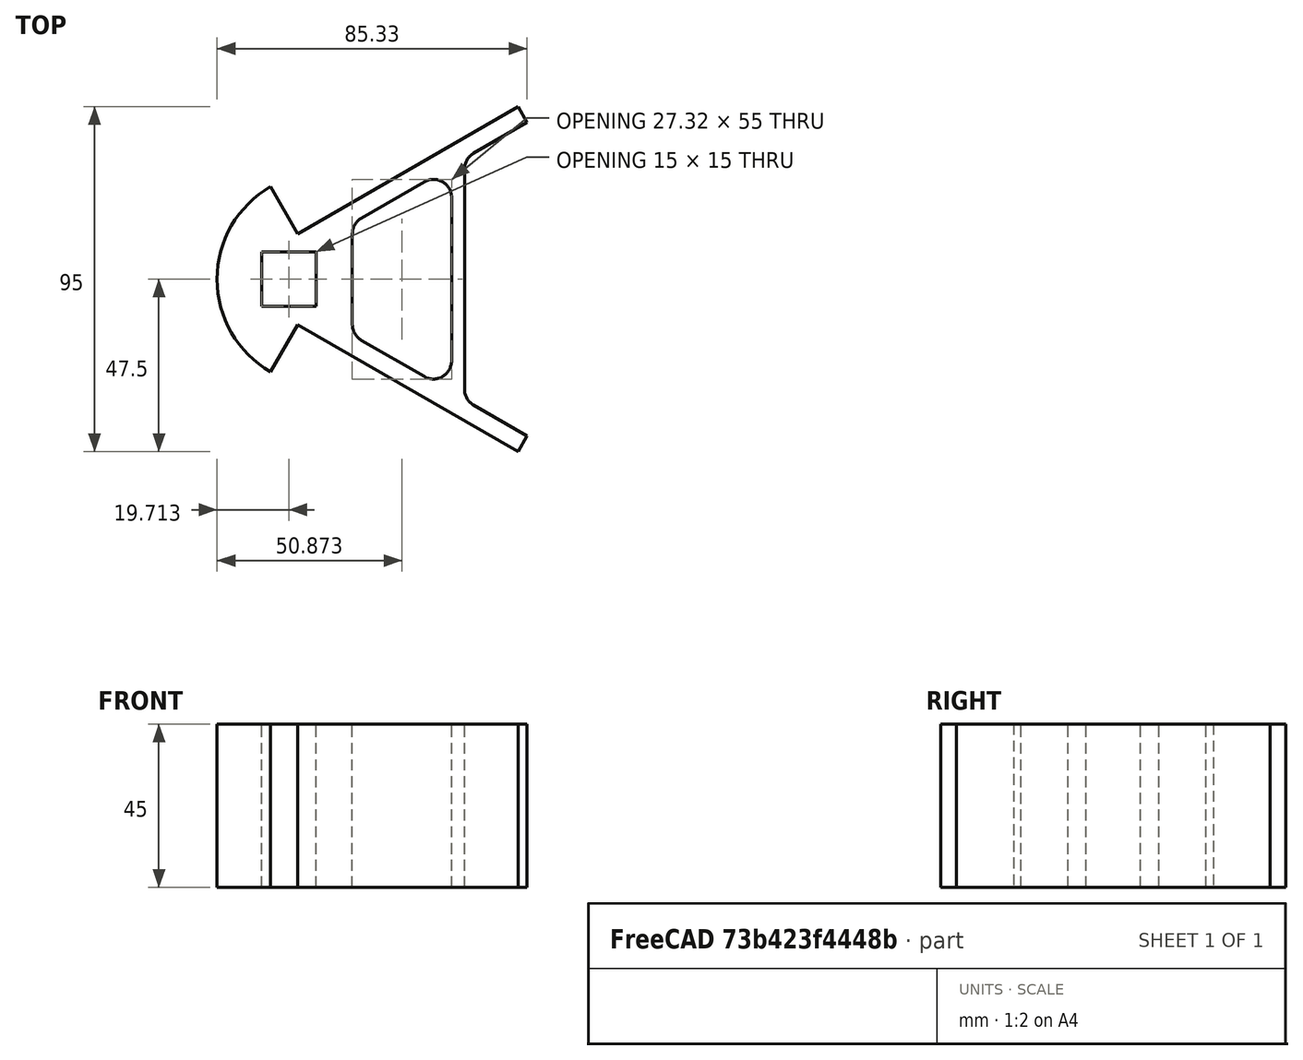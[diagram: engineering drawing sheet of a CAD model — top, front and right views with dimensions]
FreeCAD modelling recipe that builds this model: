
FCSTD DOCUMENT
Label: BaseCorner
objects: Sketcher::SketchObject×1, PartDesign::Pad×1
note: 3 computed .brp shape members not serialized (recipe doc carries the construction recipe); baked Part::Feature solids carry a one-line shape summary decoded from their .brp

FEATURE [Sketcher::SketchObject] Sketch
  sketch-geometry (32):
    g0: LineSegment StartX=-7.21688 StartY=60 StartZ=0 EndX=53.4049 EndY=95 EndZ=0
    g1: LineSegment StartX=-7.21688 StartY=35 StartZ=0 EndX=53.4049 EndY=0 EndZ=0
    g2: LineSegment StartX=53.4049 StartY=95 StartZ=0 EndX=55.9049 EndY=90.6699 EndZ=0
    g3: LineSegment StartX=53.4049 StartY=0 StartZ=0 EndX=55.9049 EndY=4.33013 EndZ=0
    g4: LineSegment StartX=55.9049 StartY=90.6699 StartZ=0 EndX=41.1552 EndY=82.1541 EndZ=0
    g5: LineSegment StartX=41.1552 StartY=12.8459 StartZ=0 EndX=55.9049 EndY=4.33013 EndZ=0
    g6: LineSegment StartX=27.6036 StartY=20.6699 StartZ=0 EndX=10.2831 EndY=30.6699 EndZ=0
    g7: LineSegment StartX=10.2831 StartY=64.3301 StartZ=0 EndX=27.6036 EndY=74.3301 EndZ=0
    g8: LineSegment [constr] StartX=27.6036 StartY=74.3301 StartZ=0 EndX=41.1552 EndY=82.1541 EndZ=0
    g9: LineSegment [constr] StartX=27.6036 StartY=20.6699 StartZ=0 EndX=41.1552 EndY=12.8459 EndZ=0
    g10: ArcOfCircle CenterX=30.1036 CenterY=70 CenterZ=0 NormalX=0 NormalY=0 NormalZ=1 Radius=5 StartAngle=1.02985e-06 EndAngle=2.09439
    g11: ArcOfCircle CenterX=30.1036 CenterY=25 CenterZ=0 NormalX=0 NormalY=0 NormalZ=1 Radius=5 StartAngle=4.18879 EndAngle=6.28318
    g12: LineSegment StartX=35.1036 StartY=70 StartZ=0 EndX=35.1036 EndY=25 EndZ=0
    g13: ArcOfCircle CenterX=12.7831 CenterY=60 CenterZ=0 NormalX=0 NormalY=0 NormalZ=1 Radius=5 StartAngle=2.09439 EndAngle=3.14159
    g14: ArcOfCircle CenterX=12.7831 CenterY=35 CenterZ=0 NormalX=0 NormalY=0 NormalZ=1 Radius=5 StartAngle=3.14159 EndAngle=4.1888
    g15: LineSegment StartX=7.7831 StartY=60 StartZ=0 EndX=7.7831 EndY=35 EndZ=0
    g16: LineSegment [constr] StartX=-14.7169 StartY=72.9904 StartZ=0 EndX=45.9049 EndY=107.99 EndZ=0
    g17: LineSegment [constr] StartX=45.9049 StartY=107.99 StartZ=0 EndX=53.4049 EndY=95 EndZ=0
    g18: LineSegment StartX=-7.21688 StartY=60 StartZ=0 EndX=-14.7169 EndY=72.9904 EndZ=0
    g19: LineSegment StartX=-7.21688 StartY=35 StartZ=0 EndX=-14.7169 EndY=22.0096 EndZ=0
    g20: ArcOfCircle CenterX=0 CenterY=47.5 CenterZ=0 NormalX=0 NormalY=0 NormalZ=1 Radius=29.4338 StartAngle=2.0944 EndAngle=4.18879
    g21: LineSegment [constr] StartX=-7.21688 StartY=60 StartZ=0 EndX=-7.21688 EndY=35 EndZ=0
    g22: LineSegment [constr] StartX=-7.21688 StartY=35 StartZ=0 EndX=7.7831 EndY=35 EndZ=0
    g23: ArcOfCircle CenterX=43.6552 CenterY=77.824 CenterZ=0 NormalX=0 NormalY=0 NormalZ=1 Radius=5 StartAngle=2.0944 EndAngle=3.14159
    g24: ArcOfCircle CenterX=43.6552 CenterY=17.176 CenterZ=0 NormalX=0 NormalY=0 NormalZ=1 Radius=5 StartAngle=3.14159 EndAngle=4.18879
    g25: LineSegment StartX=38.6552 StartY=77.824 StartZ=0 EndX=38.6552 EndY=17.176 EndZ=0
    g26: LineSegment StartX=-17.2169 StartY=55 StartZ=0 EndX=-2.2169 EndY=55 EndZ=0
    g27: LineSegment StartX=-2.2169 StartY=40 StartZ=0 EndX=-17.2169 EndY=40 EndZ=0
    g28: LineSegment StartX=-17.2169 StartY=40 StartZ=0 EndX=-17.2169 EndY=55 EndZ=0
    g29: LineSegment StartX=-2.2169 StartY=55 StartZ=0 EndX=-2.2169 EndY=47.5 EndZ=0
    g30: LineSegment StartX=-2.2169 StartY=47.5 StartZ=0 EndX=-2.2169 EndY=40 EndZ=0
    g31: LineSegment [constr] StartX=0 StartY=47.5 StartZ=0 EndX=-2.2169 EndY=47.5 EndZ=0
  constraints (97):
    c: Coincident(g2,g0)
    c: Coincident(g3,g1)
    c: Perpendicular(g3,g1)
    c: Perpendicular(g2,g0)
    c: Coincident(g4,g2)
    c: Coincident(g5,g3)
    c: Parallel(g5,g1)
    c: Parallel(g4,g0)
    c: Equal(g0,g1)
    c: Equal(g2,g3)
    c: Angle(g0) = 0.523599
    c: Distance(g3) = 5
    c: Coincident(g8,g4)
    c: Parallel(g5,g9)
    c: Parallel(g9,g6)
    c: Parallel(g7,g8)
    c: Parallel(g8,g4)
    c: Angle(g1) = -0.523599
    c: Coincident(g8,g7)
    c: Coincident(g6,g9)
    c: Coincident(g10,g7)
    c: Coincident(g11,g6)
    c: Coincident(g12,g10)
    c: Coincident(g12,g11)
    c: Tangent(g10,g12)
    c: Tangent(g11,g12)
    c: Tangent(g11,g6)
    c: Tangent(g10,g7)
    c: Vertical(g12)
    c: Equal(g10,g11)
    c: Coincident(g13,g7)
    c: Coincident(g14,g6)
    c: Coincident(g15,g13)
    c: Coincident(g15,g14)
    c: Vertical(g15)
    c: Tangent(g15,g13)
    c: Tangent(g14,g15)
    c: Tangent(g13,g7)
    c: Tangent(g14,g6)
    c: Equal(g10,g13)
    c: Equal(g13,g14)
    c: Coincident(g16,g17)
    c: Coincident(g17,g0)
    c: Perpendicular(g16,g17)
    c: Parallel(g2,g17)
    c: Distance(g17) = 15
    c: DistanceY(g12) = -45
    c: Coincident(g18,g0)
    c: Coincident(g19,g1)
    c: Perpendicular(g19,g1)
    c: Perpendicular(g0,g18)
    c: Coincident(g16,g18)
    c: Equal(g19,g18)
    c: Coincident(g20,g16)
    c: Coincident(g20,g19)
    c: Tangent(g16,g20)
    c: Coincident(g21,g0)
    c: Coincident(g21,g1)
    c: Vertical(g21)
    c: DistanceY(g21) = -25
    c: Distance(g16) = 70
    c: Coincident(g22,g1)
    c: Coincident(g22,g14)
    c: Horizontal(g22)
    c: Coincident(g23,g4)
    c: Coincident(g24,g5)
    c: Coincident(g25,g23)
    c: Coincident(g25,g24)
    c: Vertical(g25)
    c: DistanceX(g11,g24) = 3.55159
    c: Tangent(g24,g25)
    c: Tangent(g5,g24)
    c: Coincident(g5,g9)
    c: Tangent(g23,g25)
    c: Tangent(g4,g23)
    c: Equal(g23,g24)
    c: Equal(g24,g10)
    c: Radius(g10) = 5
    c: DistanceY(g1) = 0
    c: DistanceX(g20) = 0
    c: Coincident(g27,g28)
    c: Coincident(g28,g26)
    c: Horizontal(g26)
    c: Horizontal(g27)
    c: Vertical(g28)
    c: Coincident(g29,g26)
    c: Vertical(g29)
    c: Coincident(g29,g30)
    c: Coincident(g30,g27)
    c: Vertical(g30)
    c: Equal(g30,g29)
    c: Coincident(g31,g20)
    c: Coincident(g31,g29)
    c: Horizontal(g31)
    c: Equal(g28,g27)
    c: DistanceY(g28) = 15
    c: DistanceX(g27,g14) = 10
FEATURE [PartDesign::Pad] Pad
  Length = 45
  MirroredExtent = false
  Sketch = -> Sketch
